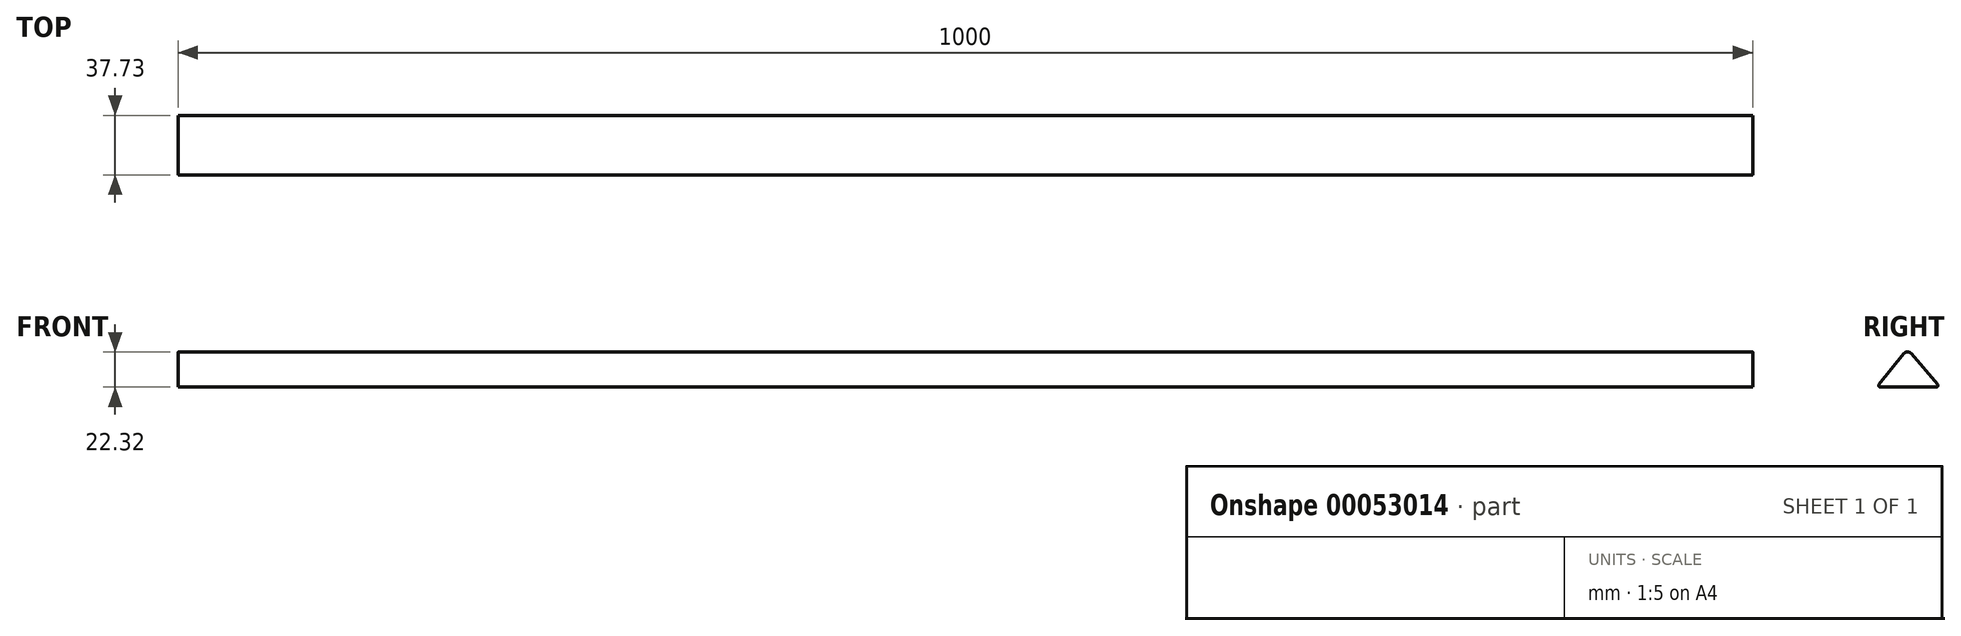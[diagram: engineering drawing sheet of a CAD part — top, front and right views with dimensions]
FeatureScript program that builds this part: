
annotation { "Feature Type Name" : "Feature", "Feature Type Description" : "" }
export const myFeature = defineFeature(function(context is Context, id is Id, definition is map)
    precondition{}
    {
        {
            var Q0;
            Q0=qCreatedBy(makeId("Right.planeOp"),FACE);
            var sketch = newSketch(context, id + "F0", { "sketchPlane" : qUnion([Q0])});
            skLineSegment(sketch, "E0", {"start": v(-2.27, -2.8) * mm, "end": v(-18.1, -22.38) * mm});
            skLineSegment(sketch, "E1", {"start": v(-17.31, -24.01) * mm, "end": v(18.42, -24.01) * mm});
            skLineSegment(sketch, "E2", {"start": v(19.18, -22.36) * mm, "end": v(2.35, -2.74) * mm});
            skPoint(sketch, "E3.visualSharp", {"position": v(0, 0) * mm});
            skArc(sketch, "E3.filletArc", {"start": v(2.35, -2.74) * mm, "mid": v(0.02, -1.69) * mm, "end": v(-2.27, -2.8) * mm});
            skPoint(sketch, "E4.visualSharp", {"position": v(20.6, -24.01) * mm});
            skArc(sketch, "E4.filletArc", {"start": v(18.42, -24.01) * mm, "mid": v(19.32, -23.43) * mm, "end": v(19.18, -22.36) * mm});
            skPoint(sketch, "E5.visualSharp", {"position": v(-19.4, -24.01) * mm});
            skArc(sketch, "E5.filletArc", {"start": v(-18.1, -22.38) * mm, "mid": v(-18.22, -23.44) * mm, "end": v(-17.31, -24.01) * mm});
            skSolve(sketch);
        }
        {
            var Q0;
            Q0=makeQuery(id+"F0.imprint","IMPRINT",FACE,{"disambiguationData":[TD([[makeQuery(id+"F0.imprint","IMPRINT",EDGE,{"derivedFrom":sQuery(id+"F0.wireOp",EDGE,"E0")}),1.0]])]});
            extrude(context, id + "F1", {"entities" : qUnion([Q0]), "endBound" : BoundingType.SYMMETRIC, "depth" : 1000 * mm});
        }
    });
